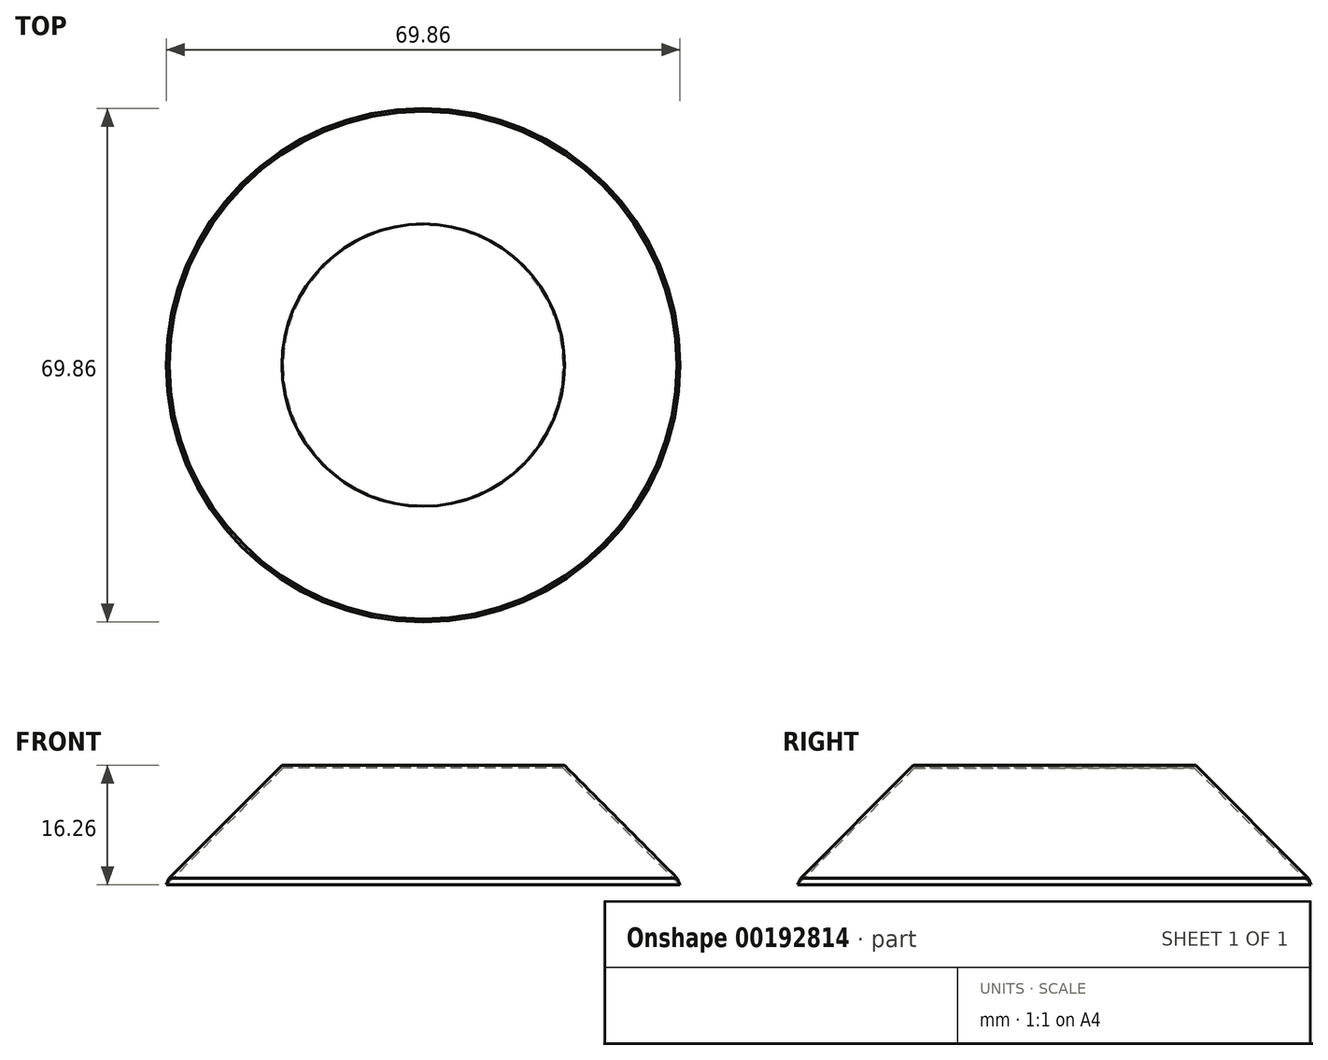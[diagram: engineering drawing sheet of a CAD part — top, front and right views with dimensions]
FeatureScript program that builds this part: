
annotation { "Feature Type Name" : "Feature", "Feature Type Description" : "" }
export const myFeature = defineFeature(function(context is Context, id is Id, definition is map)
    precondition{}
    {
        {
            var Q0;
            Q0=qCreatedBy(makeId("Front.planeOp"),FACE);
            var sketch = newSketch(context, id + "F0", { "sketchPlane" : qUnion([Q0])});
            skLineSegment(sketch, "E0", {"start": v(0, 15.87) * mm, "end": v(19.05, 15.87) * mm});
            skLineSegment(sketch, "E1", {"start": v(19.05, 15.87) * mm, "end": v(34.93, 0) * mm});
            skLineSegment(sketch, "E2", {"start": v(0, 15.87) * mm, "end": v(0, 0) * mm});
            skLineSegment(sketch, "E3", {"start": v(0, 0) * mm, "end": v(34.93, 0) * mm});
            skLineSegment(sketch, "E4.0", {"start": v(19.2, 16.26) * mm, "end": v(34.53, 0.93) * mm});
            skLineSegment(sketch, "E4.1", {"start": v(0, 16.26) * mm, "end": v(19.2, 16.26) * mm});
            skLineSegment(sketch, "E5", {"start": v(34.93, 0) * mm, "end": v(34.53, 0.93) * mm});
            skLineSegment(sketch, "E6", {"start": v(0, 16.26) * mm, "end": v(0, 15.87) * mm});
            skSolve(sketch);
        }
        {
            var Q0;
            Q0=makeQuery(id+"F0.imprint","IMPRINT",FACE,{"disambiguationData":[TD([[makeQuery(id+"F0.imprint","IMPRINT",EDGE,{"derivedFrom":sQuery(id+"F0.wireOp",EDGE,"E0")}),1.0]])]});
            var Q1;
            Q1=sQuery(id+"F0.wireOp",EDGE,"E2");
            revolve(context, id + "F1", {"entities" : qUnion([Q0]), "axis" : qUnion([Q1]), "revolveType" : RevolveType.FULL});
        }
    });
